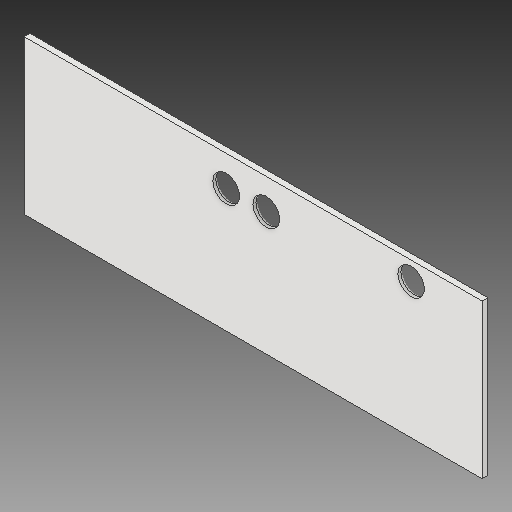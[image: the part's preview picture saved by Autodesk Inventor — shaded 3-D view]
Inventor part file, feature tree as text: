
AUTODESK INVENTOR PART (.ipt)
format: ipt  version: 2017 (Build 210142000, 142)  size: 115,712 bytes
history: native  units: in
note: dims shown in document units (in); Inventor stores cm internally (conversion verified against a paired STEP export)
features: other x5, reference x3, extrude x2, sketch x2, fillet x1
ambient origin geometry x8: Origin, YZ Plane, XZ Plane, XY Plane, X Axis, Y Axis, Z Axis, Center Point
bodies: Solid1 (feature_tree)
feature tree (13):
  extrude  "Extrusion1"  Depth=1.725in
  extrude  "Extrusion2"  Depth=0.0312in
  fillet  "Fillet1"  Radius=0.1378in
  sketch  "Sketch1"  dims[d0=5.133in d1=1.725in]
  sketch  "Sketch2"  dims[d2=0.065in d3=0.0in d4=0.02in d5=0.1378in d6=0.081in d7=0.081in d8=0.065in d9=0.0in d10=0.0312in]
  reference  "Reference1"
  reference  "Reference2"
  reference  "Reference3"
  parser-record x1  (decoder bookkeeping rows leaked as tree rows — omitted from the tree; the rows remain in map.json)
  other  "main_assy.iam"
  other  "CUI_PJ-002B:1"
  other  "Tactile switch Omron_B3F:1"
  other  "Tactile switch Omron_B3F:2"
note: 1 file-system path scrubbed to <path> (originals preserved in map.json)
